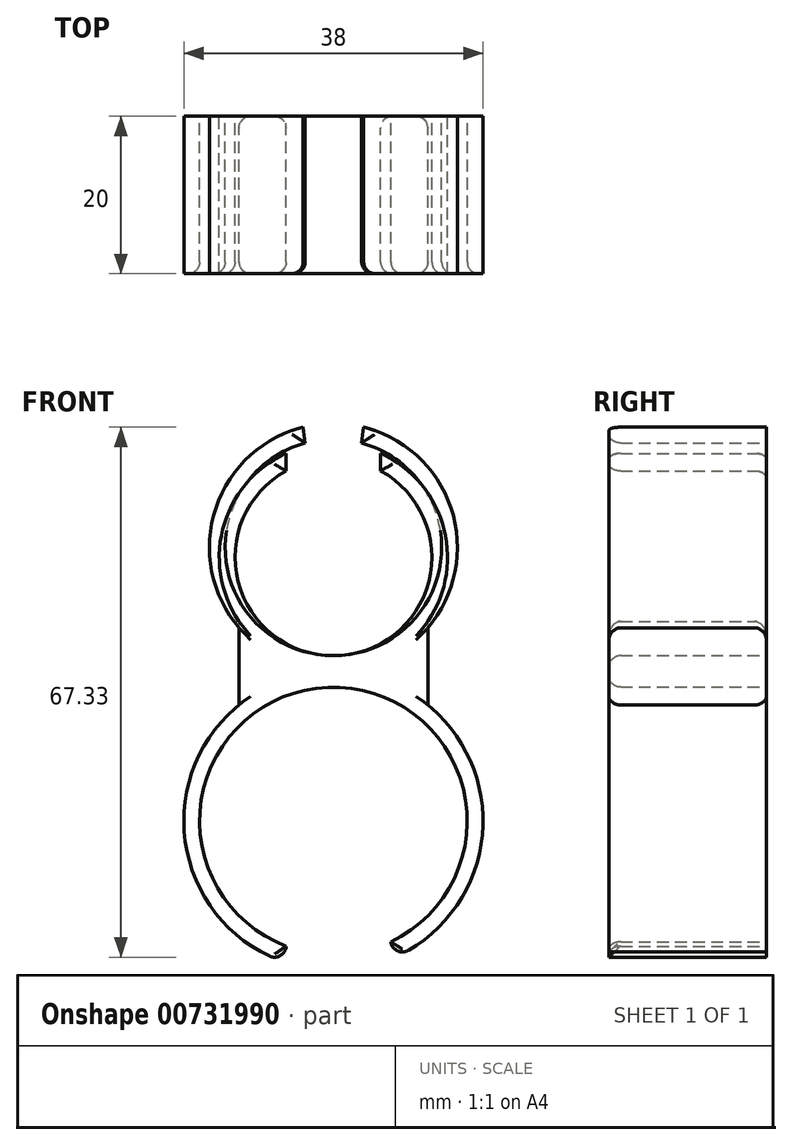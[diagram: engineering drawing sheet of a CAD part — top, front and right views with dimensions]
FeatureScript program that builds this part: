
annotation { "Feature Type Name" : "Feature", "Feature Type Description" : "" }
export const myFeature = defineFeature(function(context is Context, id is Id, definition is map)
    precondition{}
    {
        {
            var Q0;
            Q0=qCreatedBy(makeId("Front.planeOp"),FACE);
            var sketch = newSketch(context, id + "F0", { "sketchPlane" : qUnion([Q0])});
            skArc(sketch, "E0", {"start": v(7.29, -15.36) * mm, "mid": v(-0.7, 16.99) * mm, "end": v(-6, -15.9) * mm});
            skArc(sketch, "E1", {"start": v(-12, 14.73) * mm, "mid": v(-18.69, -3.42) * mm, "end": v(-6, -18.03) * mm});
            skArc(sketch, "E2", {"start": v(-3.59, 48.02) * mm, "mid": v(0, 21) * mm, "end": v(3.59, 48.02) * mm});
            skArc(sketch, "E3", {"start": v(12, 24.55) * mm, "mid": v(15, 39.55) * mm, "end": v(3.84, 50.02) * mm});
            skArc(sketch, "E4", {"start": v(12, 25.36) * mm, "mid": v(13.96, 37.42) * mm, "end": v(6, 46.7) * mm});
            skArc(sketch, "E5", {"start": v(-6, 44.47) * mm, "mid": v(0, 21) * mm, "end": v(6, 44.47) * mm});
            skLineSegment(sketch, "E6", {"start": v(-12, 14.73) * mm, "end": v(-12, 25.36) * mm});
            skLineSegment(sketch, "E7", {"start": v(12, 14.73) * mm, "end": v(12, 25.36) * mm});
            skArc(sketch, "E8.trimOffspring", {"start": v(-3.84, 50.02) * mm, "mid": v(-15, 39.55) * mm, "end": v(-12, 24.55) * mm});
            skLineSegment(sketch, "E9.trimOffspring", {"start": v(-6, 46.7) * mm, "end": v(-6, 44.47) * mm});
            skLineSegment(sketch, "E10.trimOffspring", {"start": v(6, 46.7) * mm, "end": v(6, 44.47) * mm});
            skArc(sketch, "E11.trimOffspring", {"start": v(-6, 46.7) * mm, "mid": v(-13.96, 37.42) * mm, "end": v(-12, 25.36) * mm});
            skLineSegment(sketch, "E12.trimOffspring", {"start": v(-6, -15.9) * mm, "end": v(-6, -18.03) * mm});
            skLineSegment(sketch, "E13.trimOffspring", {"start": v(7.29, -15.36) * mm, "end": v(7.3, -17.54) * mm});
            skArc(sketch, "E14.trimOffspring", {"start": v(7.3, -17.54) * mm, "mid": v(18.8, -2.73) * mm, "end": v(12, 14.73) * mm});
            skLineSegment(sketch, "E15", {"start": v(-3.84, 50.02) * mm, "end": v(-3.59, 48.02) * mm});
            skLineSegment(sketch, "E16", {"start": v(3.84, 50.02) * mm, "end": v(3.59, 48.02) * mm});
            skSolve(sketch);
        }
        {
            var Q0;
            Q0=makeQuery(id+"F0.imprint","IMPRINT",FACE,{"disambiguationData":[TD([[makeQuery(id+"F0.imprint","IMPRINT",EDGE,{"derivedFrom":sQuery(id+"F0.wireOp",EDGE,"E0")}),-1.0]])]});
            var Q1;
            {var subQ0=sQuery(id+"F0.wireOp",EDGE,"E3");Q1=makeQuery(id+"F0.imprint","IMPRINT",FACE,{"disambiguationData":[TD([[makeQuery(id+"F0.imprint","IMPRINT",EDGE,{"derivedFrom":subQ0}),1.0]])]});}
            var Q2;
            {var subQ5=sQuery(id+"F0.wireOp",EDGE,"E8.trimOffspring");Q2=makeQuery(id+"F0.imprint","IMPRINT",FACE,{"disambiguationData":[TD([[makeQuery(id+"F0.imprint","IMPRINT",EDGE,{"derivedFrom":subQ5}),1.0]])]});}
            extrude(context, id + "F1", {"entities" : qUnion([Q0, Q1, Q2]), "depth" : 20 * mm, "offsetDistance" : 25 * mm});
        }
        {
            var Q0;
            Q0=makeQuery(id+"F1.opExtrude","CAP_EDGE",EDGE,{"disambiguationData":[OSD([sQuery(id+"F0.wireOp",EDGE,"E2"),sQuery(id+"F0.wireOp",EDGE,"pGuP3S6k-ly88-0CJb-GRpJ-TDrEQPeQzSYt")])],"isStart":false});
            var Q1;
            Q1=makeQuery(id+"F1.opExtrude","CAP_EDGE",EDGE,{"disambiguationData":[OSD([sQuery(id+"F0.wireOp",EDGE,"E6")])],"isStart":false});
            var Q2;
            Q2=makeQuery(id+"F1.opExtrude","CAP_EDGE",EDGE,{"disambiguationData":[OSD([sQuery(id+"F0.wireOp",EDGE,"E7")])],"isStart":false});
            var Q3;
            Q3=makeQuery(id+"F1.opExtrude","CAP_EDGE",EDGE,{"disambiguationData":[OSD([sQuery(id+"F0.wireOp",EDGE,"E6")])],"isStart":true});
            var Q4;
            Q4=makeQuery(id+"F1.opExtrude","CAP_EDGE",EDGE,{"disambiguationData":[OSD([sQuery(id+"F0.wireOp",EDGE,"E7")])],"isStart":true});
            var Q5;
            Q5=makeQuery(id+"F1.opExtrude","SWEPT_EDGE",EDGE,{"disambiguationData":[OSD([sQuery(id+"F0.wireOp",EDGE,"E1"),sQuery(id+"F0.wireOp",EDGE,"E12.trimOffspring")])]});
            var Q6;
            Q6=makeQuery(id+"F1.opExtrude","SWEPT_EDGE",EDGE,{"disambiguationData":[OSD([sQuery(id+"F0.wireOp",EDGE,"E13.trimOffspring"),sQuery(id+"F0.wireOp",EDGE,"E14.trimOffspring")])]});
            var Q7;
            Q7=makeQuery(id+"F1.opExtrude","CAP_EDGE",EDGE,{"disambiguationData":[OSD([sQuery(id+"F0.wireOp",EDGE,"E12.trimOffspring")])],"isStart":false});
            var Q8;
            Q8=makeQuery(id+"F1.opExtrude","CAP_EDGE",EDGE,{"disambiguationData":[OSD([sQuery(id+"F0.wireOp",EDGE,"E13.trimOffspring")])],"isStart":false});
            var Q9;
            Q9=makeQuery(id+"F1.opExtrude","CAP_EDGE",EDGE,{"disambiguationData":[OSD([sQuery(id+"F0.wireOp",EDGE,"E0")])],"isStart":false});
            var Q10;
            Q10=makeQuery(id+"F1.opExtrude","CAP_EDGE",EDGE,{"disambiguationData":[OSD([sQuery(id+"F0.wireOp",EDGE,"E16")])],"isStart":false});
            var Q11;
            Q11=makeQuery(id+"F1.opExtrude","CAP_EDGE",EDGE,{"disambiguationData":[OSD([sQuery(id+"F0.wireOp",EDGE,"E15")])],"isStart":false});
            fillet(context, id + "F2", {"entities" : qUnion([Q0, Q1, Q2, Q3, Q4, Q5, Q6, Q7, Q8, Q9, Q10, Q11]), "radius" : 1.5 * mm, "tangentPropagation" : true, "allowEdgeOverflow" : false});
        }
        {
            var Q0;
            Q0=makeQuery(id+"F0.imprint","IMPRINT",FACE,{"disambiguationData":[TD([[makeQuery(id+"F0.imprint","IMPRINT",EDGE,{"derivedFrom":sQuery(id+"F0.wireOp",EDGE,"E0")}),-1.0]])]});
            var Q1;
            {var subQ5=sQuery(id+"F0.wireOp",EDGE,"E9.trimOffspring");Q1=makeQuery(id+"F0.imprint","IMPRINT",FACE,{"disambiguationData":[TD([[makeQuery(id+"F0.imprint","IMPRINT",EDGE,{"derivedFrom":subQ5}),-1.0]])]});}
            var Q2;
            {var subQ5=sQuery(id+"F0.wireOp",EDGE,"E10.trimOffspring");Q2=makeQuery(id+"F0.imprint","IMPRINT",FACE,{"disambiguationData":[TD([[makeQuery(id+"F0.imprint","IMPRINT",EDGE,{"derivedFrom":subQ5}),1.0]])]});}
            extrude(context, id + "F3", {"entities" : qUnion([Q0, Q1, Q2]), "depth" : 20 * mm, "offsetDistance" : 25 * mm});
        }
        {
            var Q0;
            Q0=makeQuery(id+"F3.opExtrude","CAP_EDGE",EDGE,{"disambiguationData":[OSD([sQuery(id+"F0.wireOp",EDGE,"E6")])],"isStart":true});
            var Q1;
            Q1=makeQuery(id+"F3.opExtrude","CAP_EDGE",EDGE,{"disambiguationData":[OSD([sQuery(id+"F0.wireOp",EDGE,"E7")])],"isStart":true});
            var Q2;
            Q2=makeQuery(id+"F3.opExtrude","CAP_EDGE",EDGE,{"disambiguationData":[OSD([sQuery(id+"F0.wireOp",EDGE,"E10.trimOffspring")])],"isStart":true});
            var Q3;
            Q3=makeQuery(id+"F3.opExtrude","CAP_EDGE",EDGE,{"disambiguationData":[OSD([sQuery(id+"F0.wireOp",EDGE,"E9.trimOffspring")])],"isStart":true});
            var Q4;
            Q4=makeQuery(id+"F3.opExtrude","CAP_EDGE",EDGE,{"disambiguationData":[OSD([sQuery(id+"F0.wireOp",EDGE,"E7")])],"isStart":false});
            var Q5;
            Q5=makeQuery(id+"F3.opExtrude","CAP_EDGE",EDGE,{"disambiguationData":[OSD([sQuery(id+"F0.wireOp",EDGE,"E6")])],"isStart":false});
            var Q6;
            Q6=makeQuery(id+"F3.opExtrude","SWEPT_EDGE",EDGE,{"disambiguationData":[OSD([sQuery(id+"F0.wireOp",EDGE,"E1"),sQuery(id+"F0.wireOp",EDGE,"E12.trimOffspring")])]});
            var Q7;
            Q7=makeQuery(id+"F3.opExtrude","SWEPT_EDGE",EDGE,{"disambiguationData":[OSD([sQuery(id+"F0.wireOp",EDGE,"E13.trimOffspring"),sQuery(id+"F0.wireOp",EDGE,"E14.trimOffspring")])]});
            var Q8;
            Q8=makeQuery(id+"F3.opExtrude","CAP_EDGE",EDGE,{"disambiguationData":[OSD([sQuery(id+"F0.wireOp",EDGE,"E13.trimOffspring")])],"isStart":false});
            var Q9;
            Q9=makeQuery(id+"F3.opExtrude","CAP_EDGE",EDGE,{"disambiguationData":[OSD([sQuery(id+"F0.wireOp",EDGE,"E12.trimOffspring")])],"isStart":false});
            var Q10;
            Q10=makeQuery(id+"F3.opExtrude","CAP_EDGE",EDGE,{"disambiguationData":[OSD([sQuery(id+"F0.wireOp",EDGE,"E5")])],"isStart":false});
            var Q11;
            Q11=makeQuery(id+"F3.opExtrude","CAP_EDGE",EDGE,{"disambiguationData":[OSD([sQuery(id+"F0.wireOp",EDGE,"E10.trimOffspring")])],"isStart":false});
            var Q12;
            Q12=makeQuery(id+"F3.opExtrude","CAP_EDGE",EDGE,{"disambiguationData":[OSD([sQuery(id+"F0.wireOp",EDGE,"E9.trimOffspring")])],"isStart":false});
            var Q13;
            Q13=makeQuery(id+"F3.opExtrude","CAP_EDGE",EDGE,{"disambiguationData":[OSD([sQuery(id+"F0.wireOp",EDGE,"E0")])],"isStart":false});
            fillet(context, id + "F4", {"entities" : qUnion([Q0, Q1, Q2, Q3, Q4, Q5, Q6, Q7, Q8, Q9, Q10, Q11, Q12, Q13]), "radius" : 1.5 * mm, "tangentPropagation" : true, "allowEdgeOverflow" : false});
        }
    });
